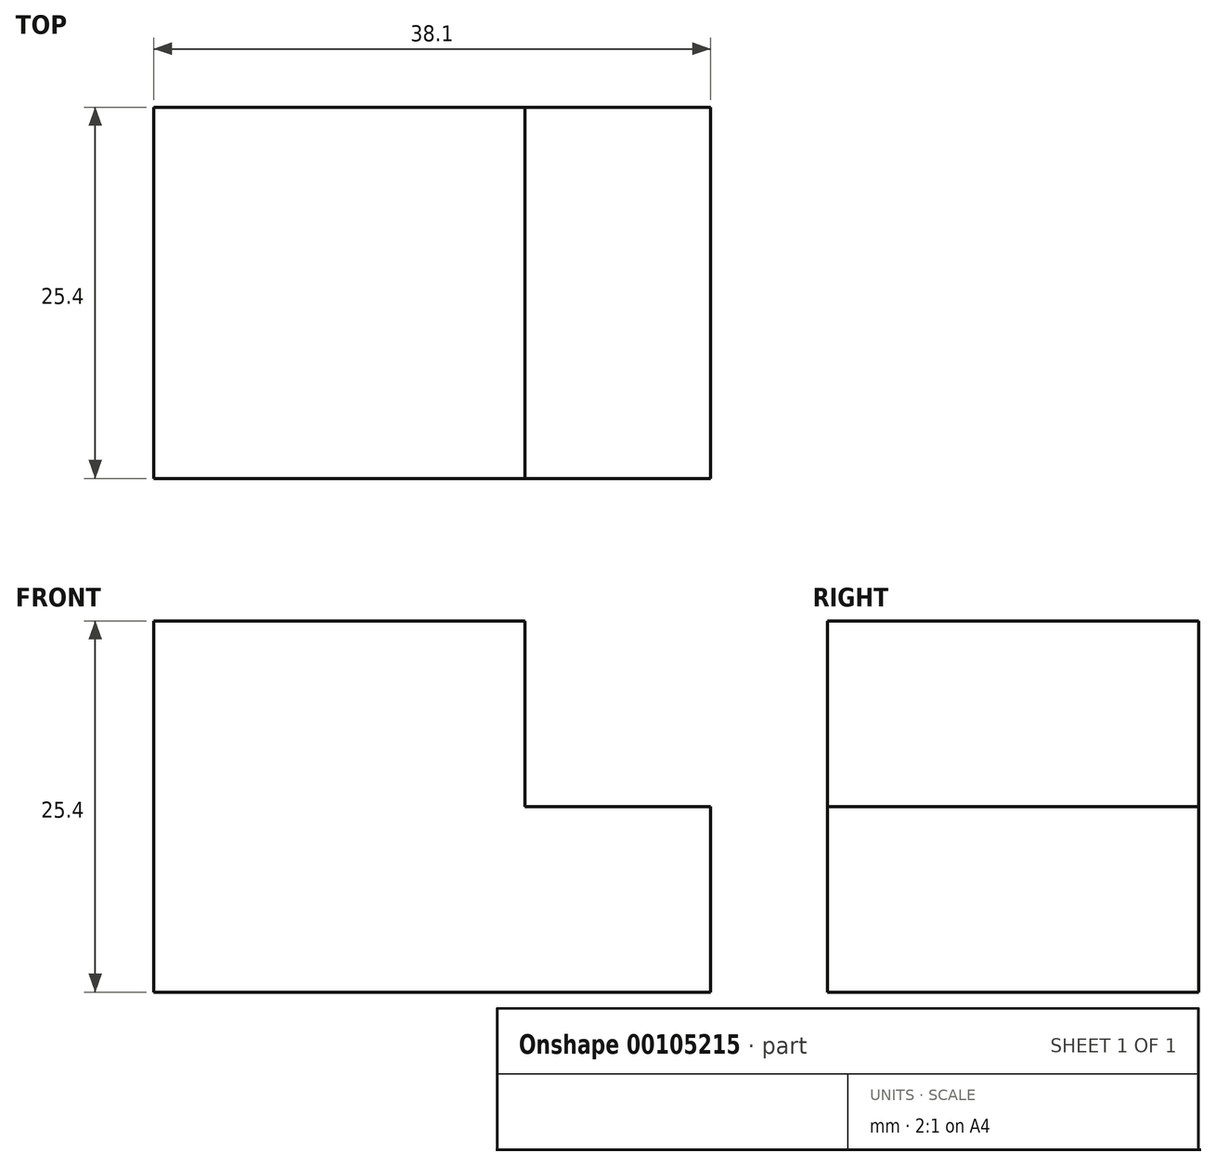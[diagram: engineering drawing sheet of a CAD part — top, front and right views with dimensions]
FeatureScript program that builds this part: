
annotation { "Feature Type Name" : "Feature", "Feature Type Description" : "" }
export const myFeature = defineFeature(function(context is Context, id is Id, definition is map)
    precondition{}
    {
        {
            var Q0;
            Q0=qCreatedBy(makeId("Front.planeOp"),FACE);
            var sketch = newSketch(context, id + "F0", { "sketchPlane" : qUnion([Q0])});
            skLineSegment(sketch, "E0", {"start": v(0, 0) * mm, "end": v(0, 25.4) * mm});
            skLineSegment(sketch, "E1", {"start": v(0, 25.4) * mm, "end": v(38.1, 25.4) * mm});
            skLineSegment(sketch, "E2", {"start": v(38.1, 25.4) * mm, "end": v(38.1, 0) * mm});
            skLineSegment(sketch, "E3", {"start": v(38.1, 0) * mm, "end": v(0, 0) * mm});
            skLineSegment(sketch, "E4", {"start": v(25.4, 25.4) * mm, "end": v(25.4, 12.7) * mm});
            skPoint(sketch, "E4.endSnap0", {"position": v(0, 12.7) * mm});
            skLineSegment(sketch, "E5", {"start": v(25.4, 12.7) * mm, "end": v(38.1, 12.7) * mm});
            skSolve(sketch);
        }
        {
            var Q0;
            {var subQ4=sQuery(id+"F0.wireOp",EDGE,"E0");Q0=makeQuery(id+"F0.imprint","IMPRINT",FACE,{"disambiguationData":[TD([[makeQuery(id+"F0.imprint","IMPRINT",EDGE,{"derivedFrom":subQ4}),-1.0]])]});}
            extrude(context, id + "F1", {"entities" : qUnion([Q0]), "depth" : 25.4 * mm});
        }
    });
